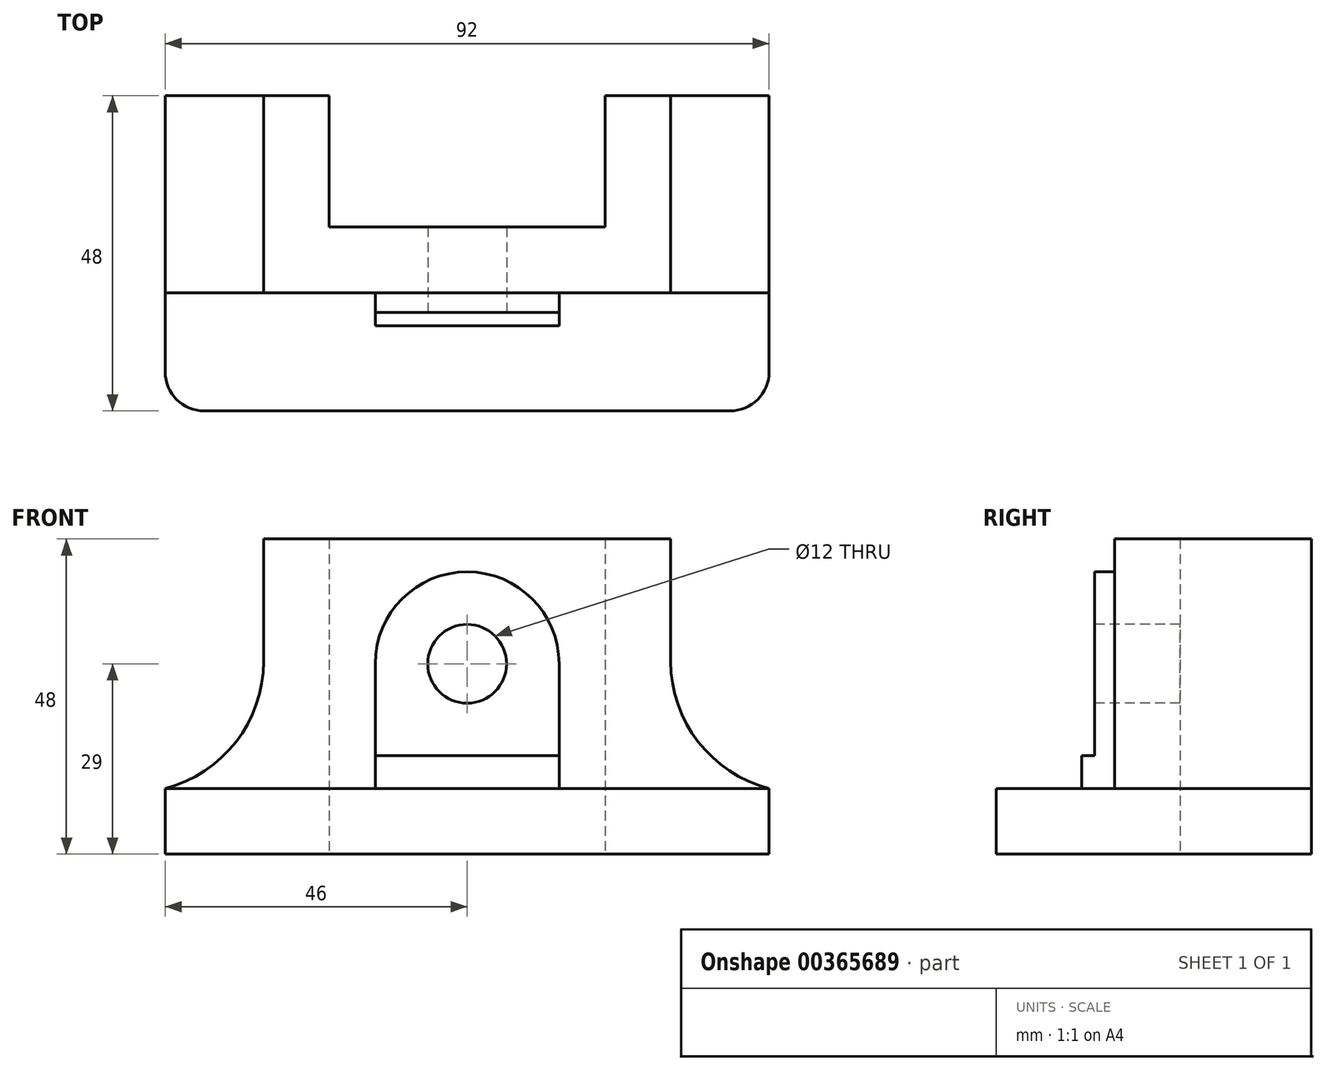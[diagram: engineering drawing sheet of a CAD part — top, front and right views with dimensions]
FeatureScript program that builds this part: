
annotation { "Feature Type Name" : "Feature", "Feature Type Description" : "" }
export const myFeature = defineFeature(function(context is Context, id is Id, definition is map)
    precondition{}
    {
        {
            var Q0;
            Q0=qCreatedBy(makeId("Top.planeOp"),FACE);
            var sketch = newSketch(context, id + "F0", { "sketchPlane" : qUnion([Q0])});
            skLineSegment(sketch, "E0", {"start": v(-46, 20) * mm, "end": v(-46, -28) * mm});
            skLineSegment(sketch, "E1", {"start": v(-46, -28) * mm, "end": v(46, -28) * mm});
            skLineSegment(sketch, "E2", {"start": v(46, -28) * mm, "end": v(46, 20) * mm});
            skLineSegment(sketch, "E3", {"start": v(46, 20) * mm, "end": v(21, 20) * mm});
            skLineSegment(sketch, "E4", {"start": v(21, 20) * mm, "end": v(21, 0) * mm});
            skLineSegment(sketch, "E5", {"start": v(21, 0) * mm, "end": v(-21, 0) * mm});
            skLineSegment(sketch, "E6", {"start": v(-21, 0) * mm, "end": v(-21, 20) * mm});
            skLineSegment(sketch, "E7", {"start": v(-21, 20) * mm, "end": v(-46, 20) * mm});
            skLineSegment(sketch, "E8", {"start": v(-31, 20) * mm, "end": v(-31, -10) * mm});
            skLineSegment(sketch, "E9", {"start": v(-31, -10) * mm, "end": v(31, -10) * mm});
            skLineSegment(sketch, "E10", {"start": v(31, 20) * mm, "end": v(31, -10) * mm});
            skSolve(sketch);
        }
        {
            var Q0;
            {var subQ1=sQuery(id+"F0.wireOp",EDGE,"E4");Q0=makeQuery(id+"F0.imprint","IMPRINT",FACE,{"disambiguationData":[TD([[makeQuery(id+"F0.imprint","IMPRINT",EDGE,{"derivedFrom":subQ1}),1.0]])]});}
            extrude(context, id + "F1", {"entities" : qUnion([Q0]), "depth" : 48 * mm});
        }
        {
            var Q0;
            Q0 = qSketchRegion(id + "F0", true);
            extrude(context, id + "F2", {"entities" : qUnion([Q0]), "operationType" : NewBodyOperationType.ADD, "depth" : 10 * mm});
        }
        {
            var Q0;
            Q0=makeQuery(id+"F2.boolean.opBoolean","INTERSECT",EDGE,{"derivedFrom":[makeQuery(id+"F1.opExtrude","SWEPT_FACE",FACE,{"disambiguationData":[OSD([sQuery(id+"F0.wireOp",EDGE,"E10")])]}),makeQuery(id+"F2.opExtrude","CAP_FACE",FACE,{"disambiguationData":[OSD([sQuery(id+"F0.wireOp",EDGE,"E0"),sQuery(id+"F0.wireOp",EDGE,"E1"),sQuery(id+"F0.wireOp",EDGE,"E2"),sQuery(id+"F0.wireOp",EDGE,"E3"),sQuery(id+"F0.wireOp",EDGE,"E4"),sQuery(id+"F0.wireOp",EDGE,"E5"),sQuery(id+"F0.wireOp",EDGE,"E6"),sQuery(id+"F0.wireOp",EDGE,"E7")])],"isStart":false})]});
            fillet(context, id + "F3", {"entities" : qUnion([Q0]), "radius" : 20 * mm, "tangentPropagation" : true, "allowEdgeOverflow" : false});
        }
        {
            var Q0;
            Q0=makeQuery(id+"F2.boolean.opBoolean","INTERSECT",EDGE,{"derivedFrom":[makeQuery(id+"F1.opExtrude","SWEPT_FACE",FACE,{"disambiguationData":[OSD([sQuery(id+"F0.wireOp",EDGE,"E8")])]}),makeQuery(id+"F2.opExtrude","CAP_FACE",FACE,{"disambiguationData":[OSD([sQuery(id+"F0.wireOp",EDGE,"E0"),sQuery(id+"F0.wireOp",EDGE,"E1"),sQuery(id+"F0.wireOp",EDGE,"E2"),sQuery(id+"F0.wireOp",EDGE,"E3"),sQuery(id+"F0.wireOp",EDGE,"E4"),sQuery(id+"F0.wireOp",EDGE,"E5"),sQuery(id+"F0.wireOp",EDGE,"E6"),sQuery(id+"F0.wireOp",EDGE,"E7")])],"isStart":false})]});
            fillet(context, id + "F4", {"entities" : qUnion([Q0]), "radius" : 20 * mm, "tangentPropagation" : true, "allowEdgeOverflow" : false});
        }
        {
            var Q0;
            Q0=makeQuery(id+"F1.opExtrude","SWEPT_FACE",FACE,{"disambiguationData":[OSD([sQuery(id+"F0.wireOp",EDGE,"E9")])]});
            var sketch = newSketch(context, id + "F5", { "sketchPlane" : qUnion([Q0])});
            skLineSegment(sketch, "E11", {"start": v(-14, 10) * mm, "end": v(-14, 29) * mm});
            skArc(sketch, "E12", {"start": v(14, 29) * mm, "mid": v(0, 43) * mm, "end": v(-14, 29) * mm});
            skLineSegment(sketch, "E13", {"start": v(14, 29) * mm, "end": v(14, 10) * mm});
            skLineSegment(sketch, "E14", {"start": v(-14, 15) * mm, "end": v(14, 15) * mm});
            skSolve(sketch);
        }
        {
            var Q0;
            Q0 = qSketchRegion(id + "F5", true);
            extrude(context, id + "F6", {"entities" : qUnion([Q0]), "operationType" : NewBodyOperationType.ADD, "depth" : 3 * mm});
        }
        {
            var Q0;
            {var subQ3=sQuery(id+"F5.wireOp",EDGE,"E14");Q0=makeQuery(id+"F5.imprint","IMPRINT",FACE,{"disambiguationData":[TD([[makeQuery(id+"F5.imprint","IMPRINT",EDGE,{"derivedFrom":subQ3}),-1.0]])]});}
            extrude(context, id + "F7", {"entities" : qUnion([Q0]), "operationType" : NewBodyOperationType.ADD, "depth" : 5 * mm});
        }
        {
            var Q0;
            Q0=makeQuery(id+"F2.opExtrude","SWEPT_EDGE",EDGE,{"disambiguationData":[OSD([sQuery(id+"F0.wireOp",EDGE,"E1"),sQuery(id+"F0.wireOp",EDGE,"E2")])]});
            fillet(context, id + "F8", {"entities" : qUnion([Q0]), "radius" : 6 * mm, "tangentPropagation" : true, "allowEdgeOverflow" : false});
        }
        {
            var Q0;
            Q0=makeQuery(id+"F2.opExtrude","SWEPT_EDGE",EDGE,{"disambiguationData":[OSD([sQuery(id+"F0.wireOp",EDGE,"E0"),sQuery(id+"F0.wireOp",EDGE,"E1")])]});
            fillet(context, id + "F9", {"entities" : qUnion([Q0]), "radius" : 6 * mm, "tangentPropagation" : true, "allowEdgeOverflow" : false});
        }
        {
            var Q0;
            Q0=makeQuery(id+"F6.opExtrude","CAP_FACE",FACE,{"disambiguationData":[OSD([sQuery(id+"F5.wireOp",EDGE,"E11"),sQuery(id+"F5.wireOp",EDGE,"E12"),sQuery(id+"F5.wireOp",EDGE,"E13"),sQuery(id+"F5.wireOp",EDGE,"E14")])],"isStart":false});
            var sketch = newSketch(context, id + "F10", { "sketchPlane" : qUnion([Q0])});
            skPoint(sketch, "E15", {"position": v(0, 29) * mm});
            skSolve(sketch);
        }
        {
            var Q0;
            Q0=sQuery(id+"F10.wireOp",VERTEX,"E15");
            var Q1;
            Q1=makeQuery(id+"F1.opExtrude","SWEPT_BODY",BODY,{"disambiguationData":[OSD([sQuery(id+"F0.wireOp",EDGE,"E3"),sQuery(id+"F0.wireOp",EDGE,"E4"),sQuery(id+"F0.wireOp",EDGE,"E5"),sQuery(id+"F0.wireOp",EDGE,"E6"),sQuery(id+"F0.wireOp",EDGE,"E7"),sQuery(id+"F0.wireOp",EDGE,"E8"),sQuery(id+"F0.wireOp",EDGE,"E9"),sQuery(id+"F0.wireOp",EDGE,"E10")])]});
            hole(context, id + "F11", {"style" : HoleStyle.SIMPLE, "endStyle" : HoleEndStyle.THROUGH, "holeDiameter" : 12 * mm, "isTappedThrough" : true, "tappedDepth" : 12 * mm, "tapClearance" : 3, "locations" : qUnion([Q0]), "scope" : qUnion([Q1])});
        }
    });
